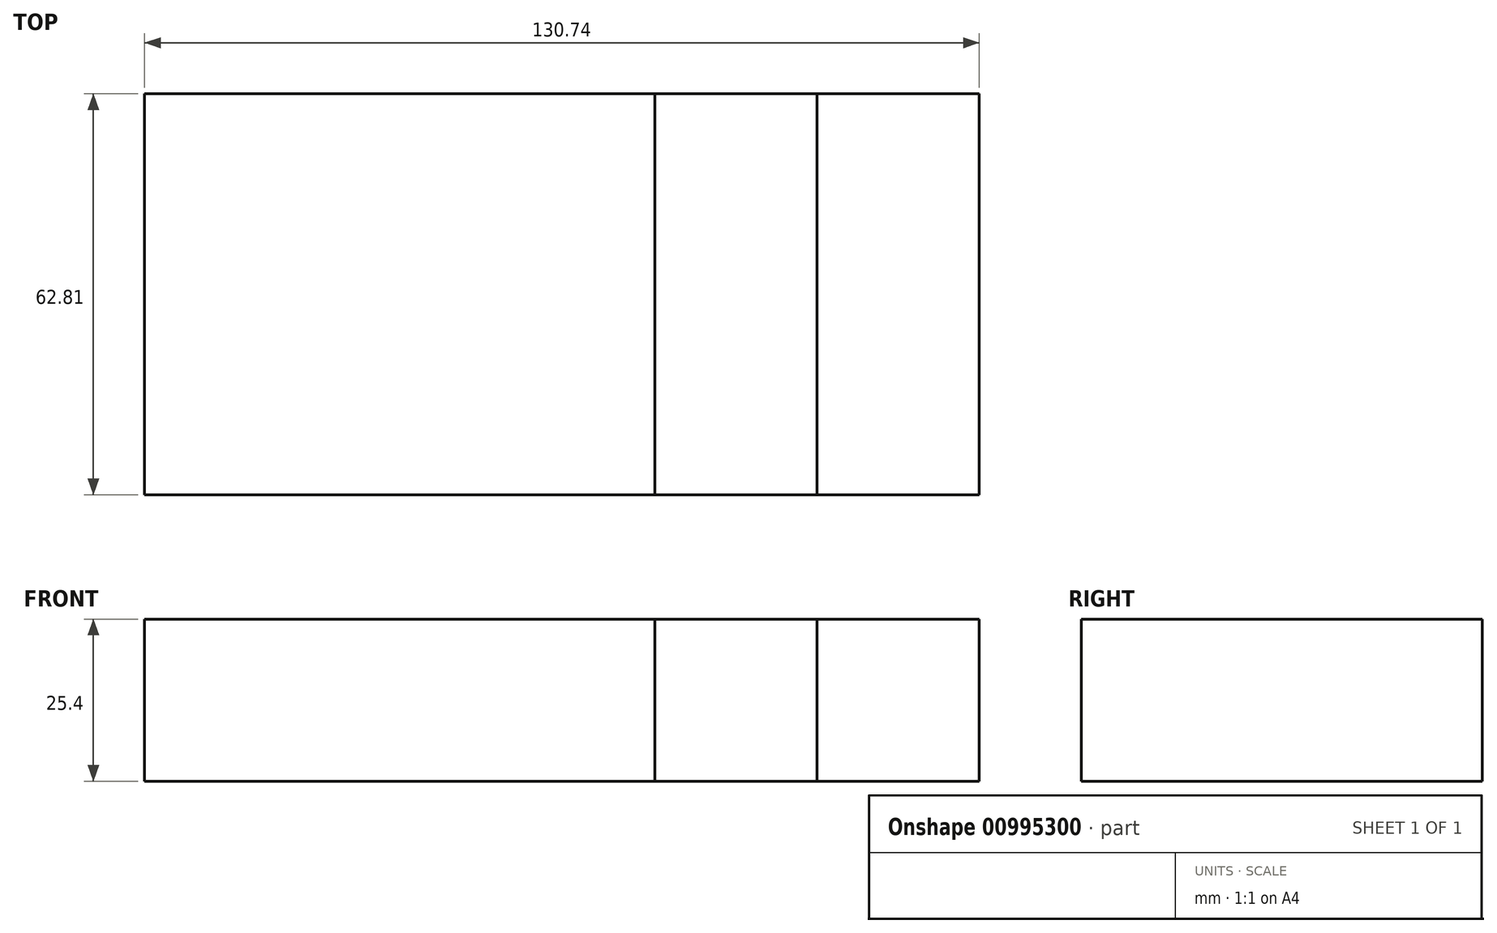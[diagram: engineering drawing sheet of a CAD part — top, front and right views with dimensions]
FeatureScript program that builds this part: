
annotation { "Feature Type Name" : "Feature", "Feature Type Description" : "" }
export const myFeature = defineFeature(function(context is Context, id is Id, definition is map)
    precondition{}
    {
        {
            var Q0;
            Q0=qCreatedBy(makeId("Top.planeOp"),FACE);
            var sketch = newSketch(context, id + "F0", { "sketchPlane" : qUnion([Q0])});
            skLineSegment(sketch, "E0.bottom", {"start": v(-30.99, 26.47) * mm, "end": v(48.95, 26.47) * mm});
            skLineSegment(sketch, "E0.top", {"start": v(-30.99, -36.34) * mm, "end": v(48.95, -36.34) * mm});
            skLineSegment(sketch, "E0.left", {"start": v(-30.99, 26.47) * mm, "end": v(-30.99, -36.34) * mm});
            skLineSegment(sketch, "E0.right", {"start": v(48.95, 26.47) * mm, "end": v(48.95, -36.34) * mm});
            skSolve(sketch);
        }
        {
            var Q0;
            Q0=makeQuery(id+"F0.imprint","IMPRINT",FACE,{"disambiguationData":[TD([[makeQuery(id+"F0.imprint","IMPRINT",EDGE,{"derivedFrom":sQuery(id+"F0.wireOp",EDGE,"E0.bottom")}),-1.0]])]});
            extrude(context, id + "F1", {"entities" : qUnion([Q0]), "depth" : 25.4 * mm, "offsetDistance" : 25.4 * mm});
        }
        {
            var Q0;
            Q0=makeQuery(id+"F1.opExtrude","SWEPT_FACE",FACE,{"disambiguationData":[OSD([sQuery(id+"F0.wireOp",EDGE,"E0.right")])]});
            var sketch = newSketch(context, id + "F2", { "sketchPlane" : qUnion([Q0])});
            skSolve(sketch);
        }
        {
            var Q0;
            Q0=makeQuery(id+"F1.opExtrude","SWEPT_FACE",FACE,{"disambiguationData":[OSD([sQuery(id+"F0.wireOp",EDGE,"E0.right")])]});
            cPlane(context, id + "F3", {"entities" : qUnion([Q0]), "cplaneType" : CPlaneType.OFFSET, "offset" : 25.4 * mm, "width" : 152.4 * mm, "height" : 152.4 * mm});
        }
        {
            var Q0;
            Q0=qCreatedBy(id+"F3.planeOp",FACE);
            var sketch = newSketch(context, id + "F4", { "sketchPlane" : qUnion([Q0])});
            skLineSegment(sketch, "E1.0.0", {"start": v(-36.34, 0) * mm, "end": v(26.47, 0) * mm});
            skLineSegment(sketch, "E1.0.1", {"start": v(26.47, 0) * mm, "end": v(26.47, 25.4) * mm});
            skLineSegment(sketch, "E1.0.2", {"start": v(26.47, 25.4) * mm, "end": v(-36.34, 25.4) * mm});
            skLineSegment(sketch, "E1.0.3", {"start": v(-36.34, 25.4) * mm, "end": v(-36.34, 0) * mm});
            skSolve(sketch);
        }
        {
            var Q0;
            Q0=makeQuery(id+"F4.imprint","IMPRINT",FACE,{"disambiguationData":[TD([[makeQuery(id+"F4.imprint","IMPRINT",EDGE,{"derivedFrom":sQuery(id+"F4.wireOp",EDGE,"E1.0.0")}),1.0]])]});
            extrude(context, id + "F5", {"entities" : qUnion([Q0]), "depth" : 25.4 * mm, "offsetDistance" : 25.4 * mm});
        }
        {
            var Q0;
            {var subQ0=sQuery(id+"F0.wireOp",EDGE,"E0.right");Q0=makeQuery(id+"F2.imprint","IMPRINT",FACE,{"disambiguationData":[TD([[makeQuery(id+"F2.imprint","IMPRINT",EDGE,{"derivedFrom":makeQuery(id+"F1.opExtrude","CAP_EDGE",EDGE,{"disambiguationData":[OSD([subQ0])],"isStart":true})}),-1.0]])]});}
            var Q1;
            Q1=makeQuery(id+"F5.opExtrude","SWEPT_BODY",BODY,{"disambiguationData":[OSD([sQuery(id+"F4.wireOp",EDGE,"E1.0.0"),sQuery(id+"F4.wireOp",EDGE,"E1.0.1"),sQuery(id+"F4.wireOp",EDGE,"E1.0.2"),sQuery(id+"F4.wireOp",EDGE,"E1.0.3")])]});
            extrude(context, id + "F6", {"entities" : qUnion([Q0]), "endBound" : BoundingType.UP_TO_BODY, "depth" : 25.4 * mm, "endBoundEntityBody" : qUnion([Q1]), "offsetDistance" : 25.4 * mm});
        }
    });
